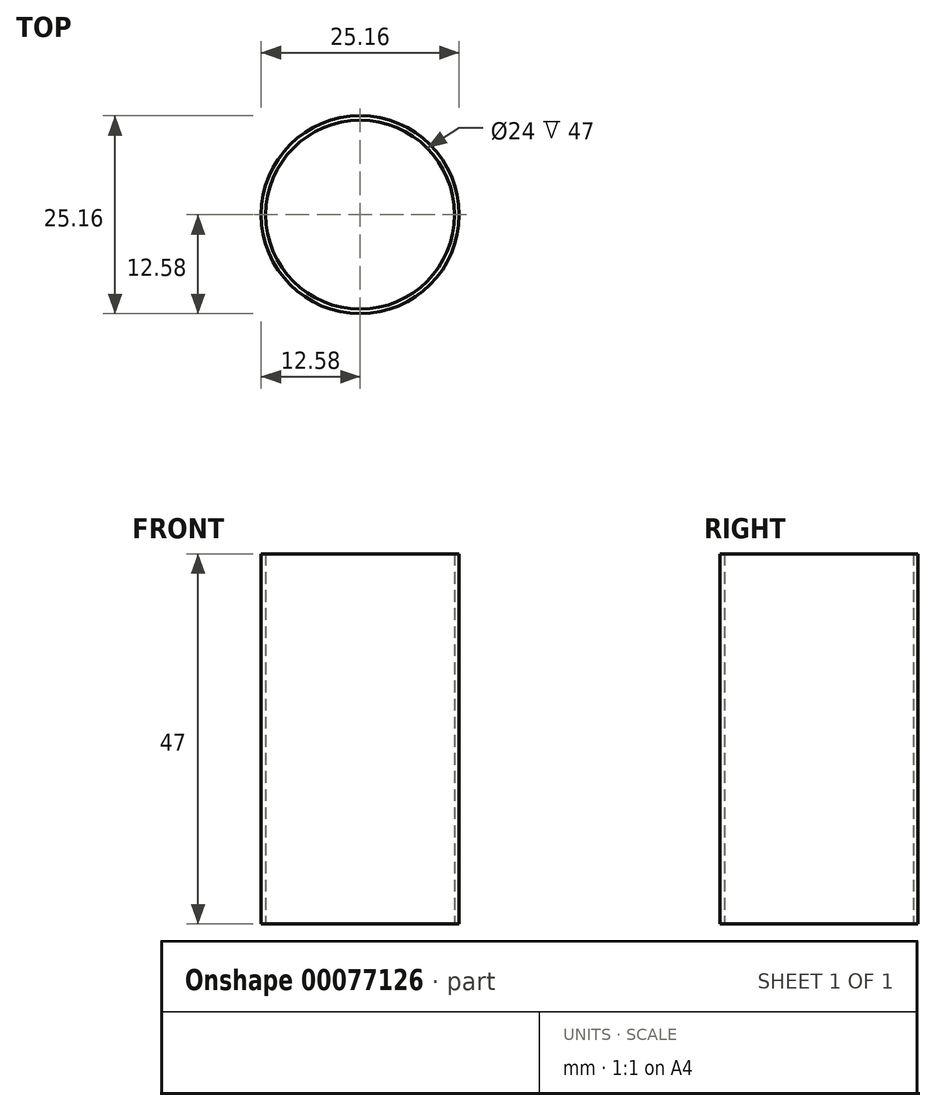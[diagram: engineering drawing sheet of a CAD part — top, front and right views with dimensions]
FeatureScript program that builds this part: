
annotation { "Feature Type Name" : "Feature", "Feature Type Description" : "" }
export const myFeature = defineFeature(function(context is Context, id is Id, definition is map)
    precondition{}
    {
        {
            var Q0;
            Q0=qCreatedBy(makeId("Top.planeOp"),FACE);
            var sketch = newSketch(context, id + "F0", { "sketchPlane" : qUnion([Q0])});
            skCircle(sketch, "E0", {"center": v(0, 0) * mm, "radius": 12.57 * mm});
            skCircle(sketch, "E1", {"center": v(0, 0) * mm, "radius": 12 * mm});
            skCircle(sketch, "E2.cCircle", {"center": v(0, 0) * mm, "radius": 12.57 * mm, "construction": true});
            skPoint(sketch, "E2.0.midPoint", {"position": v(3.99, 11.93) * mm});
            skLineSegment(sketch, "E3.0", {"start": v(-21.78, 12.57) * mm, "end": v(21.78, 12.57) * mm});
            skLineSegment(sketch, "E3.1", {"start": v(21.78, 12.58) * mm, "end": v(0, -25.15) * mm});
            skLineSegment(sketch, "E3.2", {"start": v(0, -25.15) * mm, "end": v(-21.78, 12.58) * mm});
            skPoint(sketch, "E3.0.midPoint", {"position": v(0, 12.57) * mm});
            skSolve(sketch);
        }
        {
            var Q0;
            Q0=makeQuery(id+"F0.imprint","IMPRINT",FACE,{"disambiguationData":[TD([[makeQuery(id+"F0.imprint","IMPRINT",EDGE,{"derivedFrom":sQuery(id+"F0.wireOp",EDGE,"E1")}),-1.0]])]});
            extrude(context, id + "F1", {"entities" : qUnion([Q0]), "depth" : 47 * mm, "offsetDistance" : 25 * mm, "symmetric" : true});
        }
    });
